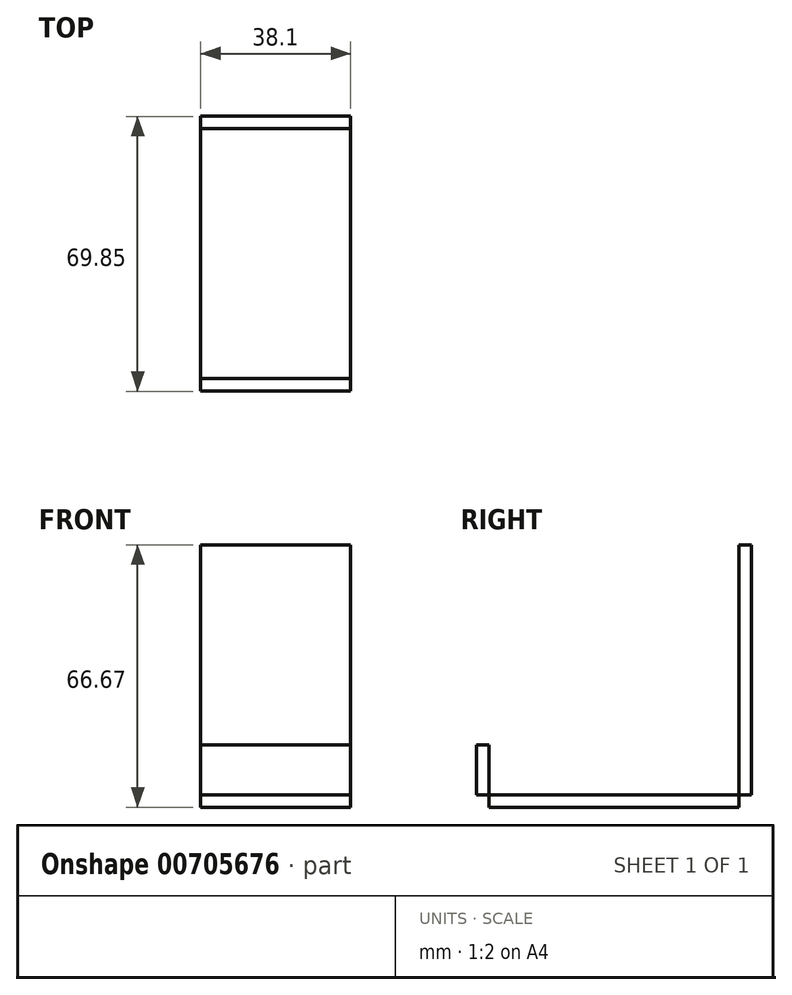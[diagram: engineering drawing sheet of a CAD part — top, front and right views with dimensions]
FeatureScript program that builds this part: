
annotation { "Feature Type Name" : "Feature", "Feature Type Description" : "" }
export const myFeature = defineFeature(function(context is Context, id is Id, definition is map)
    precondition{}
    {
        {
            var Q0;
            Q0=qCreatedBy(makeId("Top.planeOp"),FACE);
            var sketch = newSketch(context, id + "F0", { "sketchPlane" : qUnion([Q0])});
            skLineSegment(sketch, "E0.bottom", {"start": v(-47.57, 53.06) * mm, "end": v(-9.47, 53.06) * mm});
            skLineSegment(sketch, "E0.top", {"start": v(-47.57, -10.44) * mm, "end": v(-9.47, -10.44) * mm});
            skLineSegment(sketch, "E0.left", {"start": v(-47.57, 53.06) * mm, "end": v(-47.57, -10.44) * mm});
            skLineSegment(sketch, "E0.right", {"start": v(-9.47, 53.06) * mm, "end": v(-9.47, -10.44) * mm});
            skSolve(sketch);
        }
        {
            var Q0;
            Q0=makeQuery(id+"F0.imprint","IMPRINT",FACE,{"disambiguationData":[TD([[makeQuery(id+"F0.imprint","IMPRINT",EDGE,{"derivedFrom":sQuery(id+"F0.wireOp",EDGE,"E0.bottom")}),-1.0]])]});
            extrude(context, id + "F1", {"entities" : qUnion([Q0]), "depth" : 3.17 * mm, "offsetDistance" : 25.4 * mm});
        }
        {
            var Q0;
            Q0=makeQuery(id+"F1.opExtrude","CAP_FACE",FACE,{"disambiguationData":[OSD([sQuery(id+"F0.wireOp",EDGE,"E0.bottom"),sQuery(id+"F0.wireOp",EDGE,"E0.top"),sQuery(id+"F0.wireOp",EDGE,"E0.left"),sQuery(id+"F0.wireOp",EDGE,"E0.right")])],"isStart":false});
            var sketch = newSketch(context, id + "F2", { "sketchPlane" : qUnion([Q0])});
            skLineSegment(sketch, "E1.bottom", {"start": v(-47.57, 53.06) * mm, "end": v(-9.47, 53.06) * mm});
            skLineSegment(sketch, "E1.top", {"start": v(-47.57, 56.23) * mm, "end": v(-9.47, 56.23) * mm});
            skLineSegment(sketch, "E1.left", {"start": v(-47.57, 53.06) * mm, "end": v(-47.57, 56.23) * mm});
            skLineSegment(sketch, "E1.right", {"start": v(-9.47, 53.06) * mm, "end": v(-9.47, 56.23) * mm});
            skSolve(sketch);
        }
        {
            var Q0;
            Q0=makeQuery(id+"F2.imprint","IMPRINT",FACE,{"disambiguationData":[TD([[makeQuery(id+"F2.imprint","IMPRINT",EDGE,{"derivedFrom":sQuery(id+"F2.wireOp",EDGE,"E1.bottom")}),1.0]])]});
            var Q1;
            Q1=sQuery(id+"F2.wireOp",EDGE,"E1.top");
            extrude(context, id + "F3", {"entities" : qUnion([Q0]), "surfaceEntities" : qUnion([Q1]), "depth" : 63.5 * mm, "offsetDistance" : 25.4 * mm});
        }
        {
            var Q0;
            Q0=makeQuery(id+"F1.opExtrude","CAP_FACE",FACE,{"disambiguationData":[OSD([sQuery(id+"F0.wireOp",EDGE,"E0.bottom"),sQuery(id+"F0.wireOp",EDGE,"E0.top"),sQuery(id+"F0.wireOp",EDGE,"E0.left"),sQuery(id+"F0.wireOp",EDGE,"E0.right")])],"isStart":false});
            var sketch = newSketch(context, id + "F4", { "sketchPlane" : qUnion([Q0])});
            skLineSegment(sketch, "E2.bottom", {"start": v(-47.57, -10.44) * mm, "end": v(-9.47, -10.44) * mm});
            skLineSegment(sketch, "E2.top", {"start": v(-47.57, -13.62) * mm, "end": v(-9.47, -13.62) * mm});
            skLineSegment(sketch, "E2.left", {"start": v(-47.57, -10.44) * mm, "end": v(-47.57, -13.62) * mm});
            skLineSegment(sketch, "E2.right", {"start": v(-9.47, -10.44) * mm, "end": v(-9.47, -13.62) * mm});
            skSolve(sketch);
        }
        {
            var Q0;
            Q0=makeQuery(id+"F4.imprint","IMPRINT",FACE,{"disambiguationData":[TD([[makeQuery(id+"F4.imprint","IMPRINT",EDGE,{"derivedFrom":sQuery(id+"F4.wireOp",EDGE,"E2.bottom")}),-1.0]])]});
            extrude(context, id + "F5", {"entities" : qUnion([Q0]), "depth" : 12.7 * mm, "offsetDistance" : 25.4 * mm});
        }
    });
